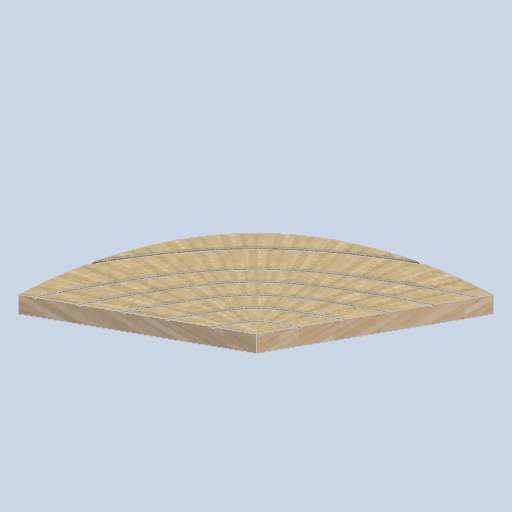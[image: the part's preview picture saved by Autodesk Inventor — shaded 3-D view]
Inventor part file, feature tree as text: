
AUTODESK INVENTOR PART (.ipt)
format: ipt  version: 2024.2 (Build 282272000, 272)  size: 862,720 bytes
history: native  units: in
note: dims shown in document units (in); Inventor stores cm internally (conversion verified against a paired STEP export)
features: sketch x19, plane x6, other x3
ambient origin geometry x8: Origin, YZ Plane, XZ Plane, XY Plane, X Axis, Y Axis, Z Axis, Center Point
bodies: Solid1 (feature_tree)
feature tree (28):
  other  "side_curve_corner_panel.ipt"
  other  "Solid1::side_curve_corner_panel.ipt"
  other  "TaggingFeature1"
  sketch  "Sketch1"  dims[d0=0.3937in]
  sketch  "Sketch2"
  sketch  "Sketch3"
  sketch  "Sketch4"
  sketch  "Sketch5"
  sketch  "Sketch6"
  sketch  "Sketch7"
  sketch  "Sketch8"
  sketch  "Sketch9"
  sketch  "Sketch10"
  sketch  "Sketch11"
  sketch  "Sketch12"
  sketch  "Sketch13"
  sketch  "Sketch14"
  sketch  "Sketch15"
  sketch  "Sketch16"
  sketch  "Sketch17"
  sketch  "Sketch18"
  sketch  "Sketch19"
  plane  "Work Plane1"
  plane  "Work Plane2"
  plane  "Work Plane3"
  plane  "Work Plane4"
  plane  "Work Plane5"
  plane  "Work Plane6"
